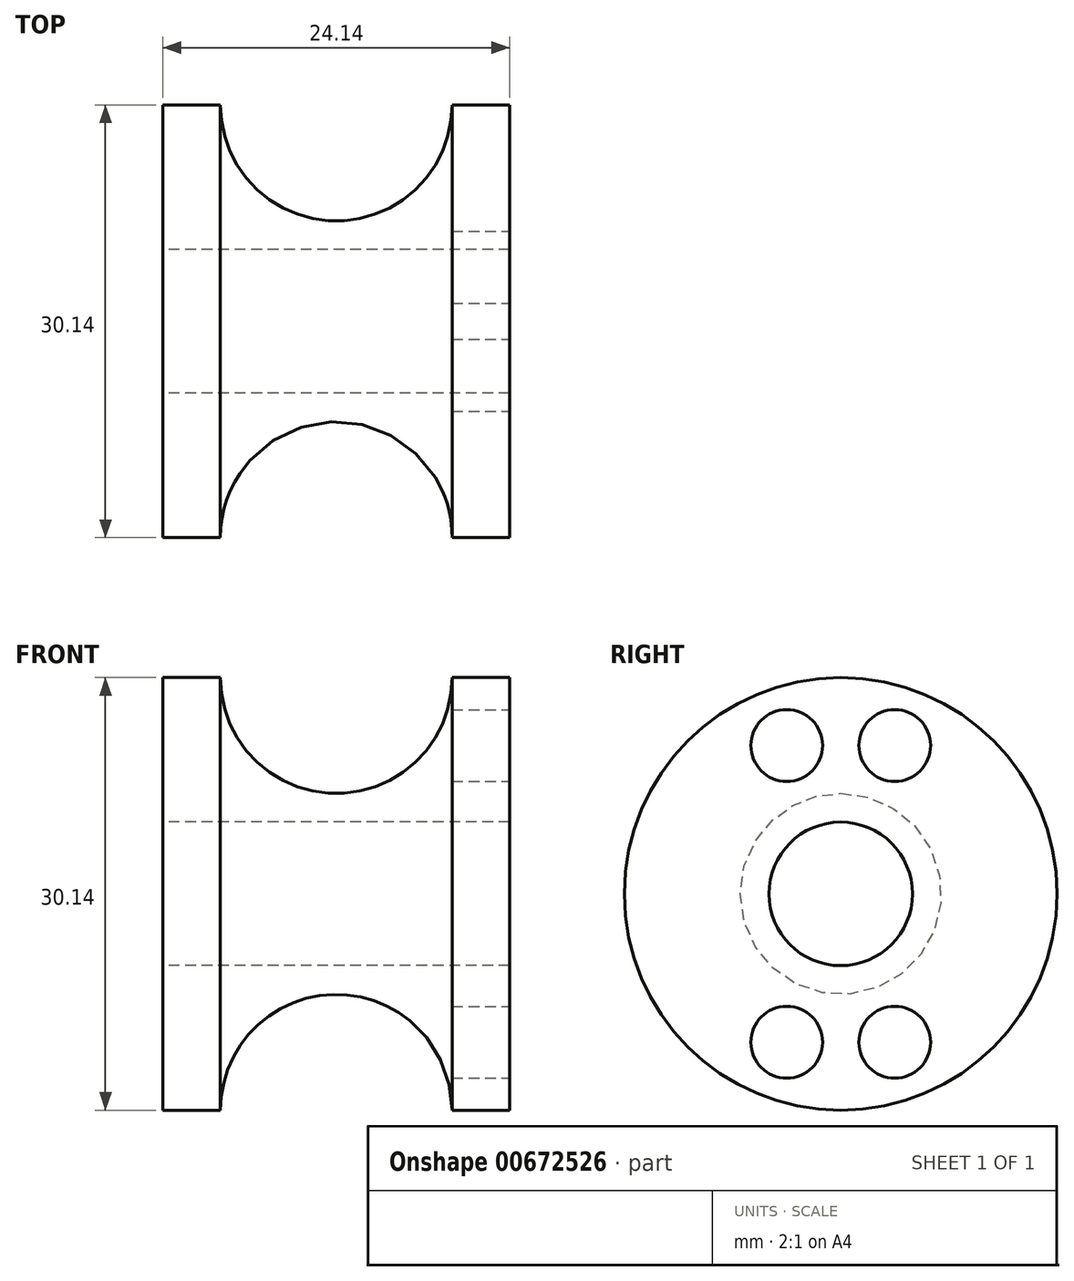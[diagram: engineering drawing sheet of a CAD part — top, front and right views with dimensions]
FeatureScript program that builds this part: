
annotation { "Feature Type Name" : "Feature", "Feature Type Description" : "" }
export const myFeature = defineFeature(function(context is Context, id is Id, definition is map)
    precondition{}
    {
        {
            var Q0;
            Q0=qCreatedBy(makeId("Top.planeOp"),FACE);
            var sketch = newSketch(context, id + "F0", { "sketchPlane" : qUnion([Q0])});
            skLineSegment(sketch, "E0", {"start": v(0, 0) * mm, "end": v(0, 7) * mm, "construction": true});
            skArc(sketch, "E1", {"start": v(0, 7) * mm, "mid": v(5.7, 9.36) * mm, "end": v(8.07, 15.07) * mm});
            skLineSegment(sketch, "E2", {"start": v(8.07, 15.07) * mm, "end": v(12.07, 15.07) * mm});
            skLineSegment(sketch, "E3", {"start": v(12.07, 15.07) * mm, "end": v(12.07, 5) * mm});
            skArc(sketch, "E4.MirrorCS", {"start": v(0, 7) * mm, "mid": v(-5.7, 9.36) * mm, "end": v(-8.07, 15.07) * mm});
            skLineSegment(sketch, "E5.MirrorCS", {"start": v(-8.07, 15.07) * mm, "end": v(-12.07, 15.07) * mm});
            skLineSegment(sketch, "E6.MirrorCS", {"start": v(-12.07, 15.07) * mm, "end": v(-12.07, 5) * mm});
            skLineSegment(sketch, "E7", {"start": v(12.07, 5) * mm, "end": v(-12.07, 5) * mm});
            skPoint(sketch, "E8.orphan", {"position": v(-12.07, 0) * mm});
            skPoint(sketch, "E9.MirrorCS.end.orphan", {"position": v(0, 0) * mm});
            skPoint(sketch, "E10.orphan", {"position": v(12.07, 0) * mm});
            skLineSegment(sketch, "E11", {"start": v(0, 0) * mm, "end": v(6.67, 0) * mm, "construction": true});
            skSolve(sketch);
        }
        {
            var Q0;
            Q0=makeQuery(id+"F0.imprint","IMPRINT",FACE,{"disambiguationData":[TD([[makeQuery(id+"F0.imprint","IMPRINT",EDGE,{"derivedFrom":sQuery(id+"F0.wireOp",EDGE,"E1")}),-1.0]])]});
            var Q1;
            Q1=sQuery(id+"F0.wireOp",EDGE,"E11");
            revolve(context, id + "F1", {"entities" : qUnion([Q0]), "axis" : qUnion([Q1]), "revolveType" : RevolveType.FULL});
        }
        {
            var Q0;
            Q0=makeQuery(id+"F1.opRevolve","SWEPT_FACE",FACE,{"disambiguationData":[OSD([sQuery(id+"F0.wireOp",EDGE,"E3")])]});
            var sketch = newSketch(context, id + "F2", { "sketchPlane" : qUnion([Q0])});
            skCircle(sketch, "E12", {"center": v(0, 0) * mm, "radius": 11 * mm, "construction": true});
            skCircle(sketch, "E13", {"center": v(3.76, 10.34) * mm, "radius": 2.5 * mm});
            skLineSegment(sketch, "E14", {"start": v(0, 0) * mm, "end": v(0, 11) * mm, "construction": true});
            skLineSegment(sketch, "E15", {"start": v(0, 0) * mm, "end": v(3.76, 10.34) * mm, "construction": true});
            skCircle(sketch, "E16.MirrorC", {"center": v(-3.76, 10.34) * mm, "radius": 2.5 * mm});
            skLineSegment(sketch, "E17", {"start": v(0, 0) * mm, "end": v(11, 0) * mm, "construction": true});
            skCircle(sketch, "E18.MirrorC", {"center": v(3.76, -10.34) * mm, "radius": 2.5 * mm});
            skCircle(sketch, "E19.MirrorC", {"center": v(-3.76, -10.34) * mm, "radius": 2.5 * mm});
            skSolve(sketch);
        }
        {
            var Q0;
            Q0 = qSketchRegion(id + "F2", true);
            extrude(context, id + "F3", {"entities" : qUnion([Q0]), "operationType" : NewBodyOperationType.REMOVE, "oppositeDirection" : true, "depth" : 4 * mm, "offsetDistance" : 25 * mm});
        }
    });
